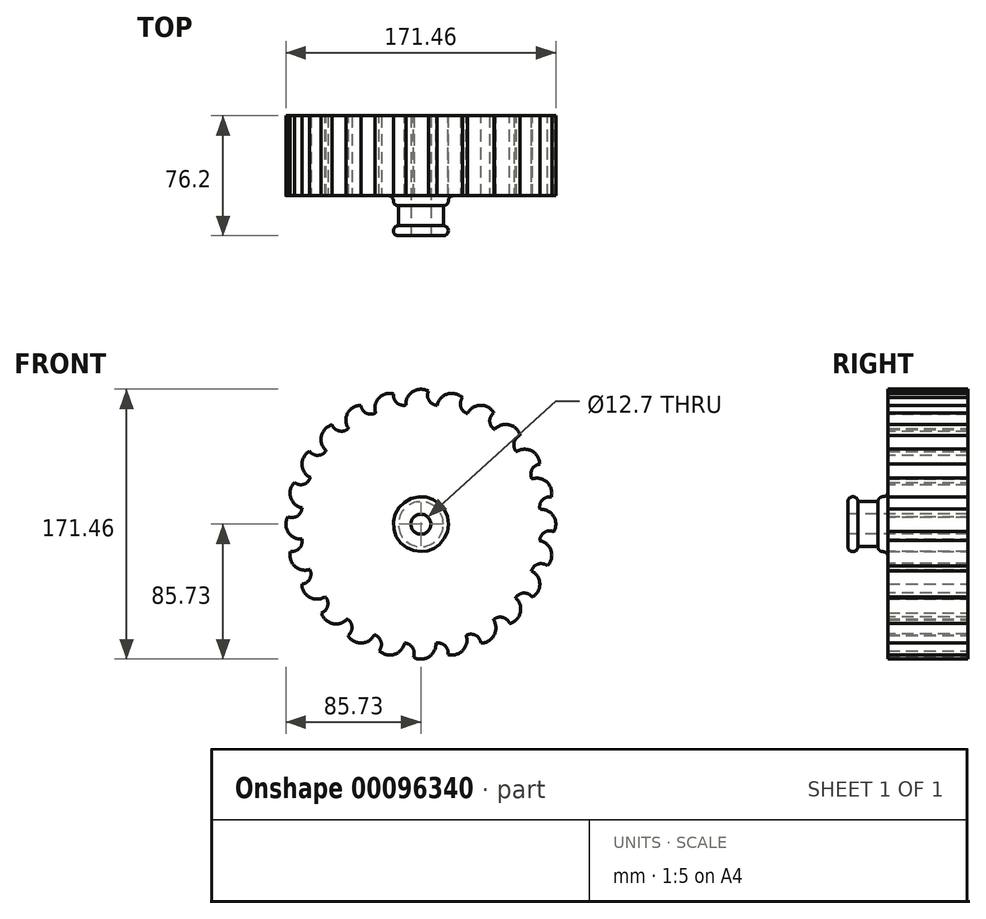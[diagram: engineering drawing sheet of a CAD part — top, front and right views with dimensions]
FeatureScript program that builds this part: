
annotation { "Feature Type Name" : "Feature", "Feature Type Description" : "" }
export const myFeature = defineFeature(function(context is Context, id is Id, definition is map)
    precondition{}
    {
        {
            var Q0;
            Q0=qCreatedBy(makeId("Front.planeOp"),FACE);
            var sketch = newSketch(context, id + "F0", { "sketchPlane" : qUnion([Q0])});
            skArc(sketch, "E0", {"start": v(-70.23, 29.57) * mm, "mid": v(-72.08, 24.7) * mm, "end": v(-73.6, 19.72) * mm});
            skLineSegment(sketch, "E1", {"start": v(0, 0) * mm, "end": v(49.4, 0) * mm, "construction": true});
            skArc(sketch, "E2", {"start": v(4.76, 84.45) * mm, "mid": v(-5.02, 84.3) * mm, "end": v(-9.5, 75.6) * mm});
            skLineSegment(sketch, "E3", {"start": v(0, 76.2) * mm, "end": v(4.76, 84.45) * mm});
            skArc(sketch, "E4.1.0", {"start": v(-17.26, 82.8) * mm, "mid": v(-26.66, 80.12) * mm, "end": v(-28.75, 70.57) * mm});
            skLineSegment(sketch, "E4.1.1", {"start": v(-19.72, 73.6) * mm, "end": v(-17.26, 82.8) * mm});
            skArc(sketch, "E4.2.0", {"start": v(-38.1, 75.52) * mm, "mid": v(-46.5, 70.5) * mm, "end": v(-46.04, 60.72) * mm});
            skLineSegment(sketch, "E4.2.1", {"start": v(-38.1, 66) * mm, "end": v(-38.1, 75.52) * mm});
            skArc(sketch, "E4.3.0", {"start": v(-56.35, 63.08) * mm, "mid": v(-63.15, 56.06) * mm, "end": v(-60.18, 46.74) * mm});
            skLineSegment(sketch, "E4.3.1", {"start": v(-53.88, 53.88) * mm, "end": v(-56.35, 63.08) * mm});
            skArc(sketch, "E4.4.0", {"start": v(-70.75, 46.35) * mm, "mid": v(-75.51, 37.8) * mm, "end": v(-70.23, 29.57) * mm});
            skLineSegment(sketch, "E4.4.1", {"start": v(-66, 38.1) * mm, "end": v(-70.75, 46.35) * mm});
            skArc(sketch, "E4.5.0", {"start": v(-80.34, 26.46) * mm, "mid": v(-82.72, 16.97) * mm, "end": v(-75.49, 10.39) * mm});
            skLineSegment(sketch, "E4.5.1", {"start": v(-73.6, 19.72) * mm, "end": v(-80.34, 26.46) * mm});
            skArc(sketch, "E4.6.0", {"start": v(-84.45, 4.76) * mm, "mid": v(-84.3, -5.02) * mm, "end": v(-75.6, -9.5) * mm});
            skLineSegment(sketch, "E4.6.1", {"start": v(-76.2, 0) * mm, "end": v(-84.45, 4.76) * mm});
            skArc(sketch, "E4.7.0", {"start": v(-82.8, -17.26) * mm, "mid": v(-80.12, -26.66) * mm, "end": v(-70.57, -28.75) * mm});
            skLineSegment(sketch, "E4.7.1", {"start": v(-73.6, -19.72) * mm, "end": v(-82.8, -17.26) * mm});
            skArc(sketch, "E4.8.0", {"start": v(-75.52, -38.1) * mm, "mid": v(-70.5, -46.5) * mm, "end": v(-60.72, -46.04) * mm});
            skLineSegment(sketch, "E4.8.1", {"start": v(-66, -38.1) * mm, "end": v(-75.52, -38.1) * mm});
            skArc(sketch, "E4.9.0", {"start": v(-63.08, -56.35) * mm, "mid": v(-56.06, -63.15) * mm, "end": v(-46.74, -60.18) * mm});
            skLineSegment(sketch, "E4.9.1", {"start": v(-53.88, -53.88) * mm, "end": v(-63.08, -56.35) * mm});
            skArc(sketch, "E4.10.0", {"start": v(-46.35, -70.75) * mm, "mid": v(-37.8, -75.51) * mm, "end": v(-29.57, -70.23) * mm});
            skLineSegment(sketch, "E4.10.1", {"start": v(-38.1, -66) * mm, "end": v(-46.35, -70.75) * mm});
            skArc(sketch, "E4.11.0", {"start": v(-26.46, -80.34) * mm, "mid": v(-16.97, -82.72) * mm, "end": v(-10.39, -75.49) * mm});
            skLineSegment(sketch, "E4.11.1", {"start": v(-19.72, -73.6) * mm, "end": v(-26.46, -80.34) * mm});
            skArc(sketch, "E4.12.0", {"start": v(-4.76, -84.45) * mm, "mid": v(5.02, -84.3) * mm, "end": v(9.5, -75.6) * mm});
            skLineSegment(sketch, "E4.12.1", {"start": v(0, -76.2) * mm, "end": v(-4.76, -84.45) * mm});
            skArc(sketch, "E4.13.0", {"start": v(17.26, -82.8) * mm, "mid": v(26.66, -80.12) * mm, "end": v(28.75, -70.57) * mm});
            skLineSegment(sketch, "E4.13.1", {"start": v(19.72, -73.6) * mm, "end": v(17.26, -82.8) * mm});
            skArc(sketch, "E4.14.0", {"start": v(38.1, -75.52) * mm, "mid": v(46.5, -70.5) * mm, "end": v(46.04, -60.72) * mm});
            skLineSegment(sketch, "E4.14.1", {"start": v(38.1, -66) * mm, "end": v(38.1, -75.52) * mm});
            skArc(sketch, "E4.15.0", {"start": v(56.35, -63.08) * mm, "mid": v(63.15, -56.06) * mm, "end": v(60.18, -46.74) * mm});
            skLineSegment(sketch, "E4.15.1", {"start": v(53.88, -53.88) * mm, "end": v(56.35, -63.08) * mm});
            skArc(sketch, "E4.16.0", {"start": v(70.75, -46.35) * mm, "mid": v(75.51, -37.8) * mm, "end": v(70.23, -29.57) * mm});
            skLineSegment(sketch, "E4.16.1", {"start": v(66, -38.1) * mm, "end": v(70.75, -46.35) * mm});
            skArc(sketch, "E4.17.0", {"start": v(80.34, -26.46) * mm, "mid": v(82.72, -16.97) * mm, "end": v(75.49, -10.39) * mm});
            skLineSegment(sketch, "E4.17.1", {"start": v(73.6, -19.72) * mm, "end": v(80.34, -26.46) * mm});
            skArc(sketch, "E4.18.0", {"start": v(84.45, -4.76) * mm, "mid": v(84.3, 5.02) * mm, "end": v(75.6, 9.5) * mm});
            skLineSegment(sketch, "E4.18.1", {"start": v(76.2, 0) * mm, "end": v(84.45, -4.76) * mm});
            skArc(sketch, "E4.19.0", {"start": v(82.8, 17.26) * mm, "mid": v(80.12, 26.66) * mm, "end": v(70.57, 28.75) * mm});
            skLineSegment(sketch, "E4.19.1", {"start": v(73.6, 19.72) * mm, "end": v(82.8, 17.26) * mm});
            skArc(sketch, "E4.20.0", {"start": v(75.52, 38.1) * mm, "mid": v(70.5, 46.5) * mm, "end": v(60.72, 46.04) * mm});
            skLineSegment(sketch, "E4.20.1", {"start": v(66, 38.1) * mm, "end": v(75.52, 38.1) * mm});
            skArc(sketch, "E4.21.0", {"start": v(63.08, 56.35) * mm, "mid": v(56.06, 63.15) * mm, "end": v(46.74, 60.18) * mm});
            skLineSegment(sketch, "E4.21.1", {"start": v(53.88, 53.88) * mm, "end": v(63.08, 56.35) * mm});
            skArc(sketch, "E4.22.0", {"start": v(46.35, 70.75) * mm, "mid": v(37.8, 75.51) * mm, "end": v(29.57, 70.23) * mm});
            skLineSegment(sketch, "E4.22.1", {"start": v(38.1, 66) * mm, "end": v(46.35, 70.75) * mm});
            skArc(sketch, "E4.23.0", {"start": v(26.46, 80.34) * mm, "mid": v(16.97, 82.72) * mm, "end": v(10.39, 75.49) * mm});
            skLineSegment(sketch, "E4.23.1", {"start": v(19.72, 73.6) * mm, "end": v(26.46, 80.34) * mm});
            skArc(sketch, "E5.trimOffspring", {"start": v(-75.49, 10.39) * mm, "mid": v(-76.02, 5.2) * mm, "end": v(-76.2, 0) * mm});
            skArc(sketch, "E6.trimOffspring", {"start": v(-75.6, -9.5) * mm, "mid": v(-74.78, -14.65) * mm, "end": v(-73.6, -19.72) * mm});
            skArc(sketch, "E7.trimOffspring", {"start": v(-70.57, -28.75) * mm, "mid": v(-68.44, -33.5) * mm, "end": v(-66, -38.1) * mm});
            skArc(sketch, "E8.trimOffspring", {"start": v(-60.72, -46.04) * mm, "mid": v(-57.44, -50.08) * mm, "end": v(-53.88, -53.88) * mm});
            skArc(sketch, "E9.trimOffspring", {"start": v(-46.74, -60.18) * mm, "mid": v(-42.52, -63.23) * mm, "end": v(-38.1, -66) * mm});
            skArc(sketch, "E10.trimOffspring", {"start": v(-29.57, -70.23) * mm, "mid": v(-24.7, -72.08) * mm, "end": v(-19.72, -73.6) * mm});
            skArc(sketch, "E11.trimOffspring", {"start": v(-10.39, -75.49) * mm, "mid": v(-5.2, -76.02) * mm, "end": v(0, -76.2) * mm});
            skArc(sketch, "E12.trimOffspring", {"start": v(9.5, -75.6) * mm, "mid": v(14.65, -74.78) * mm, "end": v(19.72, -73.6) * mm});
            skArc(sketch, "E13.trimOffspring", {"start": v(28.75, -70.57) * mm, "mid": v(33.5, -68.44) * mm, "end": v(38.1, -66) * mm});
            skArc(sketch, "E14.trimOffspring", {"start": v(46.04, -60.72) * mm, "mid": v(50.08, -57.44) * mm, "end": v(53.88, -53.88) * mm});
            skArc(sketch, "E15.trimOffspring", {"start": v(60.18, -46.74) * mm, "mid": v(63.23, -42.52) * mm, "end": v(66, -38.1) * mm});
            skArc(sketch, "E16.trimOffspring", {"start": v(70.23, -29.57) * mm, "mid": v(72.08, -24.7) * mm, "end": v(73.6, -19.72) * mm});
            skArc(sketch, "E17.trimOffspring", {"start": v(75.49, -10.39) * mm, "mid": v(76.02, -5.2) * mm, "end": v(76.2, 0) * mm});
            skArc(sketch, "E18.trimOffspring", {"start": v(75.6, 9.5) * mm, "mid": v(74.78, 14.65) * mm, "end": v(73.6, 19.72) * mm});
            skArc(sketch, "E19.trimOffspring", {"start": v(70.57, 28.75) * mm, "mid": v(68.44, 33.5) * mm, "end": v(66, 38.1) * mm});
            skArc(sketch, "E20.trimOffspring", {"start": v(60.72, 46.04) * mm, "mid": v(57.44, 50.08) * mm, "end": v(53.88, 53.88) * mm});
            skArc(sketch, "E21.trimOffspring", {"start": v(46.74, 60.18) * mm, "mid": v(42.52, 63.23) * mm, "end": v(38.1, 66) * mm});
            skArc(sketch, "E22.trimOffspring", {"start": v(29.57, 70.23) * mm, "mid": v(24.7, 72.08) * mm, "end": v(19.72, 73.6) * mm});
            skArc(sketch, "E23.trimOffspring", {"start": v(10.39, 75.49) * mm, "mid": v(5.2, 76.02) * mm, "end": v(0, 76.2) * mm});
            skArc(sketch, "E24.trimOffspring", {"start": v(-9.5, 75.6) * mm, "mid": v(-14.65, 74.78) * mm, "end": v(-19.72, 73.6) * mm});
            skArc(sketch, "E25.trimOffspring", {"start": v(-28.75, 70.57) * mm, "mid": v(-33.5, 68.44) * mm, "end": v(-38.1, 66) * mm});
            skArc(sketch, "E26.trimOffspring", {"start": v(-46.04, 60.72) * mm, "mid": v(-50.08, 57.44) * mm, "end": v(-53.88, 53.88) * mm});
            skArc(sketch, "E27.trimOffspring", {"start": v(-60.18, 46.74) * mm, "mid": v(-63.23, 42.52) * mm, "end": v(-66, 38.1) * mm});
            skSolve(sketch);
        }
        {
            var Q0;
            Q0 = qSketchRegion(id + "F0", true);
            extrude(context, id + "F1", {"entities" : qUnion([Q0]), "depth" : 50.8 * mm});
        }
        {
            var Q0;
            Q0=makeQuery(id+"F1.opExtrude","CAP_FACE",FACE,{"disambiguationData":[OSD([sQuery(id+"F0.wireOp",EDGE,"E0"),sQuery(id+"F0.wireOp",EDGE,"E2"),sQuery(id+"F0.wireOp",EDGE,"E3"),sQuery(id+"F0.wireOp",EDGE,"E4.1.0"),sQuery(id+"F0.wireOp",EDGE,"E4.1.1"),sQuery(id+"F0.wireOp",EDGE,"E4.2.0"),sQuery(id+"F0.wireOp",EDGE,"E4.2.1"),sQuery(id+"F0.wireOp",EDGE,"E4.3.0"),sQuery(id+"F0.wireOp",EDGE,"E4.3.1"),sQuery(id+"F0.wireOp",EDGE,"E4.4.0"),sQuery(id+"F0.wireOp",EDGE,"E4.4.1"),sQuery(id+"F0.wireOp",EDGE,"E4.5.0"),sQuery(id+"F0.wireOp",EDGE,"E4.5.1"),sQuery(id+"F0.wireOp",EDGE,"E4.6.0"),sQuery(id+"F0.wireOp",EDGE,"E4.6.1"),sQuery(id+"F0.wireOp",EDGE,"E4.7.0"),sQuery(id+"F0.wireOp",EDGE,"E4.7.1"),sQuery(id+"F0.wireOp",EDGE,"E4.8.0"),sQuery(id+"F0.wireOp",EDGE,"E4.8.1"),sQuery(id+"F0.wireOp",EDGE,"E4.9.0"),sQuery(id+"F0.wireOp",EDGE,"E4.9.1"),sQuery(id+"F0.wireOp",EDGE,"E4.10.0"),sQuery(id+"F0.wireOp",EDGE,"E4.10.1"),sQuery(id+"F0.wireOp",EDGE,"E4.11.0"),sQuery(id+"F0.wireOp",EDGE,"E4.11.1"),sQuery(id+"F0.wireOp",EDGE,"E4.12.0"),sQuery(id+"F0.wireOp",EDGE,"E4.12.1"),sQuery(id+"F0.wireOp",EDGE,"E4.13.0"),sQuery(id+"F0.wireOp",EDGE,"E4.13.1"),sQuery(id+"F0.wireOp",EDGE,"E4.14.0"),sQuery(id+"F0.wireOp",EDGE,"E4.14.1"),sQuery(id+"F0.wireOp",EDGE,"E4.15.0"),sQuery(id+"F0.wireOp",EDGE,"E4.15.1"),sQuery(id+"F0.wireOp",EDGE,"E4.16.0"),sQuery(id+"F0.wireOp",EDGE,"E4.16.1"),sQuery(id+"F0.wireOp",EDGE,"E4.17.0"),sQuery(id+"F0.wireOp",EDGE,"E4.17.1"),sQuery(id+"F0.wireOp",EDGE,"E4.18.0"),sQuery(id+"F0.wireOp",EDGE,"E4.18.1"),sQuery(id+"F0.wireOp",EDGE,"E4.19.0"),sQuery(id+"F0.wireOp",EDGE,"E4.19.1"),sQuery(id+"F0.wireOp",EDGE,"E4.20.0"),sQuery(id+"F0.wireOp",EDGE,"E4.20.1"),sQuery(id+"F0.wireOp",EDGE,"E4.21.0"),sQuery(id+"F0.wireOp",EDGE,"E4.21.1"),sQuery(id+"F0.wireOp",EDGE,"E4.22.0"),sQuery(id+"F0.wireOp",EDGE,"E4.22.1"),sQuery(id+"F0.wireOp",EDGE,"E4.23.0"),sQuery(id+"F0.wireOp",EDGE,"E4.23.1"),sQuery(id+"F0.wireOp",EDGE,"E5.trimOffspring"),sQuery(id+"F0.wireOp",EDGE,"E6.trimOffspring"),sQuery(id+"F0.wireOp",EDGE,"E7.trimOffspring"),sQuery(id+"F0.wireOp",EDGE,"E8.trimOffspring"),sQuery(id+"F0.wireOp",EDGE,"E9.trimOffspring"),sQuery(id+"F0.wireOp",EDGE,"E10.trimOffspring"),sQuery(id+"F0.wireOp",EDGE,"E11.trimOffspring"),sQuery(id+"F0.wireOp",EDGE,"E12.trimOffspring"),sQuery(id+"F0.wireOp",EDGE,"E13.trimOffspring"),sQuery(id+"F0.wireOp",EDGE,"E14.trimOffspring"),sQuery(id+"F0.wireOp",EDGE,"E15.trimOffspring"),sQuery(id+"F0.wireOp",EDGE,"E16.trimOffspring"),sQuery(id+"F0.wireOp",EDGE,"E17.trimOffspring"),sQuery(id+"F0.wireOp",EDGE,"E18.trimOffspring"),sQuery(id+"F0.wireOp",EDGE,"E19.trimOffspring"),sQuery(id+"F0.wireOp",EDGE,"E20.trimOffspring"),sQuery(id+"F0.wireOp",EDGE,"E21.trimOffspring"),sQuery(id+"F0.wireOp",EDGE,"E22.trimOffspring"),sQuery(id+"F0.wireOp",EDGE,"E23.trimOffspring"),sQuery(id+"F0.wireOp",EDGE,"E24.trimOffspring"),sQuery(id+"F0.wireOp",EDGE,"E25.trimOffspring"),sQuery(id+"F0.wireOp",EDGE,"E26.trimOffspring"),sQuery(id+"F0.wireOp",EDGE,"E27.trimOffspring")])],"isStart":false});
            var sketch = newSketch(context, id + "F2", { "sketchPlane" : qUnion([Q0])});
            skCircle(sketch, "E28", {"center": v(0, 0) * mm, "radius": 17.46 * mm});
            skSolve(sketch);
        }
        {
            var Q0;
            Q0 = qSketchRegion(id + "F2", true);
            extrude(context, id + "F3", {"entities" : qUnion([Q0]), "operationType" : NewBodyOperationType.ADD, "depth" : 6.35 * mm});
        }
        {
            var Q0;
            Q0=makeQuery(id+"F3.opExtrude","CAP_FACE",FACE,{"disambiguationData":[OSD([sQuery(id+"F2.wireOp",EDGE,"E28")])],"isStart":false});
            var sketch = newSketch(context, id + "F4", { "sketchPlane" : qUnion([Q0])});
            skCircle(sketch, "E29", {"center": v(0, 0) * mm, "radius": 14.29 * mm});
            skSolve(sketch);
        }
        {
            var Q0;
            Q0 = qSketchRegion(id + "F4", true);
            extrude(context, id + "F5", {"entities" : qUnion([Q0]), "operationType" : NewBodyOperationType.ADD, "depth" : 12.7 * mm});
        }
        {
            var Q0;
            Q0=makeQuery(id+"F5.opExtrude","CAP_FACE",FACE,{"disambiguationData":[OSD([sQuery(id+"F4.wireOp",EDGE,"E29")])],"isStart":false});
            var sketch = newSketch(context, id + "F6", { "sketchPlane" : qUnion([Q0])});
            skCircle(sketch, "E30", {"center": v(0, 0) * mm, "radius": 17.46 * mm});
            skSolve(sketch);
        }
        {
            var Q0;
            Q0 = qSketchRegion(id + "F6", true);
            extrude(context, id + "F7", {"entities" : qUnion([Q0]), "operationType" : NewBodyOperationType.ADD, "depth" : 6.35 * mm});
        }
        {
            var Q0;
            Q0=makeQuery(id+"F7.opExtrude","SWEPT_FACE",FACE,{"disambiguationData":[OSD([sQuery(id+"F6.wireOp",EDGE,"E30")])]});
            var Q1;
            Q1=makeQuery(id+"F3.opExtrude","SWEPT_FACE",FACE,{"disambiguationData":[OSD([sQuery(id+"F2.wireOp",EDGE,"E28")])]});
            fillet(context, id + "F8", {"entities" : qUnion([Q0, Q1]), "radius" : 3.17 * mm, "tangentPropagation" : true, "allowEdgeOverflow" : false});
        }
        {
            var Q0;
            Q0=makeQuery(id+"F7.opExtrude","CAP_FACE",FACE,{"disambiguationData":[OSD([sQuery(id+"F6.wireOp",EDGE,"E30")])],"isStart":false});
            var sketch = newSketch(context, id + "F9", { "sketchPlane" : qUnion([Q0])});
            skCircle(sketch, "E31", {"center": v(0, 0) * mm, "radius": 6.35 * mm});
            skSolve(sketch);
        }
        {
            var Q0;
            Q0 = qSketchRegion(id + "F9", true);
            extrude(context, id + "F10", {"entities" : qUnion([Q0]), "operationType" : NewBodyOperationType.REMOVE, "endBound" : BoundingType.THROUGH_ALL, "oppositeDirection" : true, "depth" : 25.4 * mm});
        }
        {
            var Q0;
            Q0=makeQuery(id+"F1.opExtrude","SWEPT_EDGE",EDGE,{"disambiguationData":[OSD([sQuery(id+"F0.wireOp",EDGE,"E4.3.1"),sQuery(id+"F0.wireOp",EDGE,"E26.trimOffspring")])]});
            var Q1;
            Q1=makeQuery(id+"F1.opExtrude","SWEPT_EDGE",EDGE,{"disambiguationData":[OSD([sQuery(id+"F0.wireOp",EDGE,"E4.2.1"),sQuery(id+"F0.wireOp",EDGE,"E25.trimOffspring")])]});
            var Q2;
            Q2=makeQuery(id+"F1.opExtrude","SWEPT_EDGE",EDGE,{"disambiguationData":[OSD([sQuery(id+"F0.wireOp",EDGE,"E4.1.1"),sQuery(id+"F0.wireOp",EDGE,"E24.trimOffspring")])]});
            var Q3;
            Q3=makeQuery(id+"F1.opExtrude","SWEPT_EDGE",EDGE,{"disambiguationData":[OSD([sQuery(id+"F0.wireOp",EDGE,"E3"),sQuery(id+"F0.wireOp",EDGE,"E23.trimOffspring")])]});
            var Q4;
            Q4=makeQuery(id+"F1.opExtrude","SWEPT_EDGE",EDGE,{"disambiguationData":[OSD([sQuery(id+"F0.wireOp",EDGE,"E4.23.1"),sQuery(id+"F0.wireOp",EDGE,"E22.trimOffspring")])]});
            var Q5;
            Q5=makeQuery(id+"F1.opExtrude","SWEPT_EDGE",EDGE,{"disambiguationData":[OSD([sQuery(id+"F0.wireOp",EDGE,"E4.22.1"),sQuery(id+"F0.wireOp",EDGE,"E21.trimOffspring")])]});
            var Q6;
            Q6=makeQuery(id+"F1.opExtrude","SWEPT_EDGE",EDGE,{"disambiguationData":[OSD([sQuery(id+"F0.wireOp",EDGE,"E4.21.1"),sQuery(id+"F0.wireOp",EDGE,"E20.trimOffspring")])]});
            var Q7;
            Q7=makeQuery(id+"F1.opExtrude","SWEPT_EDGE",EDGE,{"disambiguationData":[OSD([sQuery(id+"F0.wireOp",EDGE,"E4.20.1"),sQuery(id+"F0.wireOp",EDGE,"E19.trimOffspring")])]});
            var Q8;
            Q8=makeQuery(id+"F1.opExtrude","SWEPT_EDGE",EDGE,{"disambiguationData":[OSD([sQuery(id+"F0.wireOp",EDGE,"E4.19.1"),sQuery(id+"F0.wireOp",EDGE,"E18.trimOffspring")])]});
            var Q9;
            Q9=makeQuery(id+"F1.opExtrude","SWEPT_EDGE",EDGE,{"disambiguationData":[OSD([sQuery(id+"F0.wireOp",EDGE,"E4.18.1"),sQuery(id+"F0.wireOp",EDGE,"E17.trimOffspring")])]});
            var Q10;
            Q10=makeQuery(id+"F1.opExtrude","SWEPT_EDGE",EDGE,{"disambiguationData":[OSD([sQuery(id+"F0.wireOp",EDGE,"E4.17.1"),sQuery(id+"F0.wireOp",EDGE,"E16.trimOffspring")])]});
            var Q11;
            Q11=makeQuery(id+"F1.opExtrude","SWEPT_EDGE",EDGE,{"disambiguationData":[OSD([sQuery(id+"F0.wireOp",EDGE,"E4.16.1"),sQuery(id+"F0.wireOp",EDGE,"E15.trimOffspring")])]});
            var Q12;
            Q12=makeQuery(id+"F1.opExtrude","SWEPT_EDGE",EDGE,{"disambiguationData":[OSD([sQuery(id+"F0.wireOp",EDGE,"E4.15.1"),sQuery(id+"F0.wireOp",EDGE,"E14.trimOffspring")])]});
            var Q13;
            Q13=makeQuery(id+"F1.opExtrude","SWEPT_EDGE",EDGE,{"disambiguationData":[OSD([sQuery(id+"F0.wireOp",EDGE,"E4.14.1"),sQuery(id+"F0.wireOp",EDGE,"E13.trimOffspring")])]});
            var Q14;
            Q14=makeQuery(id+"F1.opExtrude","SWEPT_EDGE",EDGE,{"disambiguationData":[OSD([sQuery(id+"F0.wireOp",EDGE,"E4.13.1"),sQuery(id+"F0.wireOp",EDGE,"E12.trimOffspring")])]});
            var Q15;
            Q15=makeQuery(id+"F1.opExtrude","SWEPT_EDGE",EDGE,{"disambiguationData":[OSD([sQuery(id+"F0.wireOp",EDGE,"E4.12.1"),sQuery(id+"F0.wireOp",EDGE,"E11.trimOffspring")])]});
            var Q16;
            Q16=makeQuery(id+"F1.opExtrude","SWEPT_EDGE",EDGE,{"disambiguationData":[OSD([sQuery(id+"F0.wireOp",EDGE,"E4.11.1"),sQuery(id+"F0.wireOp",EDGE,"E10.trimOffspring")])]});
            var Q17;
            Q17=makeQuery(id+"F1.opExtrude","SWEPT_EDGE",EDGE,{"disambiguationData":[OSD([sQuery(id+"F0.wireOp",EDGE,"E4.10.1"),sQuery(id+"F0.wireOp",EDGE,"E9.trimOffspring")])]});
            var Q18;
            Q18=makeQuery(id+"F1.opExtrude","SWEPT_EDGE",EDGE,{"disambiguationData":[OSD([sQuery(id+"F0.wireOp",EDGE,"E4.9.1"),sQuery(id+"F0.wireOp",EDGE,"E8.trimOffspring")])]});
            var Q19;
            Q19=makeQuery(id+"F1.opExtrude","SWEPT_EDGE",EDGE,{"disambiguationData":[OSD([sQuery(id+"F0.wireOp",EDGE,"E4.8.1"),sQuery(id+"F0.wireOp",EDGE,"E7.trimOffspring")])]});
            var Q20;
            Q20=makeQuery(id+"F1.opExtrude","SWEPT_EDGE",EDGE,{"disambiguationData":[OSD([sQuery(id+"F0.wireOp",EDGE,"E4.7.1"),sQuery(id+"F0.wireOp",EDGE,"E6.trimOffspring")])]});
            var Q21;
            Q21=makeQuery(id+"F1.opExtrude","SWEPT_EDGE",EDGE,{"disambiguationData":[OSD([sQuery(id+"F0.wireOp",EDGE,"E4.6.1"),sQuery(id+"F0.wireOp",EDGE,"E5.trimOffspring")])]});
            var Q22;
            Q22=makeQuery(id+"F1.opExtrude","SWEPT_EDGE",EDGE,{"disambiguationData":[OSD([sQuery(id+"F0.wireOp",EDGE,"E0"),sQuery(id+"F0.wireOp",EDGE,"E4.5.1")])]});
            var Q23;
            Q23=makeQuery(id+"F1.opExtrude","SWEPT_EDGE",EDGE,{"disambiguationData":[OSD([sQuery(id+"F0.wireOp",EDGE,"E4.4.1"),sQuery(id+"F0.wireOp",EDGE,"E27.trimOffspring")])]});
            fillet(context, id + "F11", {"entities" : qUnion([Q0, Q1, Q2, Q3, Q4, Q5, Q6, Q7, Q8, Q9, Q10, Q11, Q12, Q13, Q14, Q15, Q16, Q17, Q18, Q19, Q20, Q21, Q22, Q23]), "radius" : 6.35 * mm, "tangentPropagation" : true, "allowEdgeOverflow" : false});
        }
    });
